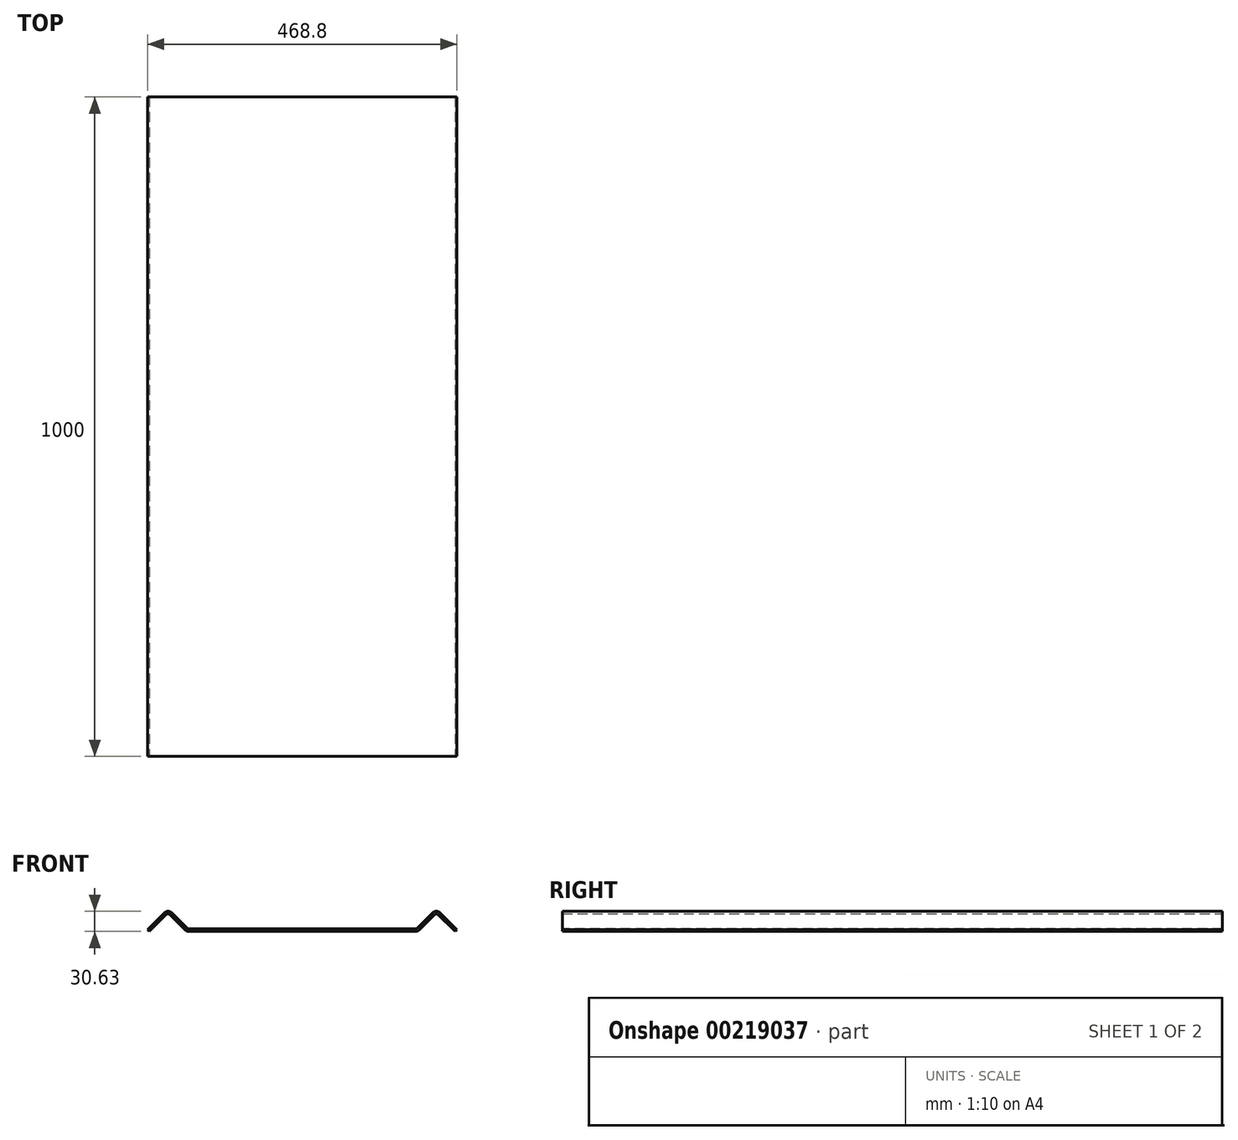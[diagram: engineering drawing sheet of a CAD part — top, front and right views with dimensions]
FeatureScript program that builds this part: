
annotation { "Feature Type Name" : "Feature", "Feature Type Description" : "" }
export const myFeature = defineFeature(function(context is Context, id is Id, definition is map)
    precondition{}
    {
        {
            var Q0;
            Q0=qCreatedBy(makeId("Front.planeOp"),FACE);
            var sketch = newSketch(context, id + "F0", { "sketchPlane" : qUnion([Q0])});
            skLineSegment(sketch, "E0", {"start": v(0, 0) * mm, "end": v(-175, 0) * mm});
            skLineSegment(sketch, "E1", {"start": v(-175, 0) * mm, "end": v(-203.28, 28.28) * mm});
            skLineSegment(sketch, "E2", {"start": v(-203.28, 28.28) * mm, "end": v(-231.57, 0) * mm});
            skLineSegment(sketch, "E3.0", {"start": v(-203.28, 33.94) * mm, "end": v(-234.4, 2.83) * mm});
            skLineSegment(sketch, "E3.1", {"start": v(-173.34, 4) * mm, "end": v(-203.28, 33.94) * mm});
            skLineSegment(sketch, "E3.2", {"start": v(0, 4) * mm, "end": v(-173.34, 4) * mm});
            skLineSegment(sketch, "E4", {"start": v(-231.57, 0) * mm, "end": v(-234.4, 2.83) * mm});
            skLineSegment(sketch, "E5", {"start": v(0, 0) * mm, "end": v(0, 19.74) * mm, "construction": true});
            skLineSegment(sketch, "E6.MirrorCS", {"start": v(231.57, 0) * mm, "end": v(234.4, 2.83) * mm});
            skLineSegment(sketch, "E7.MirrorCS", {"start": v(175, 0) * mm, "end": v(203.28, 28.28) * mm});
            skLineSegment(sketch, "E8.MirrorCS", {"start": v(203.28, 28.28) * mm, "end": v(231.57, 0) * mm});
            skLineSegment(sketch, "E9.MirrorCS", {"start": v(173.34, 4) * mm, "end": v(203.28, 33.94) * mm});
            skLineSegment(sketch, "E10.MirrorCS", {"start": v(0, 0) * mm, "end": v(175, 0) * mm});
            skLineSegment(sketch, "E11.MirrorCS", {"start": v(0, 4) * mm, "end": v(173.34, 4) * mm});
            skLineSegment(sketch, "E12.MirrorCS", {"start": v(203.28, 33.94) * mm, "end": v(234.4, 2.83) * mm});
            skSolve(sketch);
        }
        {
            var Q0;
            Q0 = qSketchRegion(id + "F0", true);
            extrude(context, id + "F1", {"entities" : qUnion([Q0]), "oppositeDirection" : true, "depth" : 1000 * mm});
        }
        {
            var Q0;
            Q0=makeQuery(id+"F1.opExtrude","SWEPT_EDGE",EDGE,{"disambiguationData":[OSD([sQuery(id+"F0.wireOp",EDGE,"E1"),sQuery(id+"F0.wireOp",EDGE,"E2")])]});
            var Q1;
            Q1=makeQuery(id+"F1.opExtrude","SWEPT_EDGE",EDGE,{"disambiguationData":[OSD([sQuery(id+"F0.wireOp",EDGE,"E7.MirrorCS"),sQuery(id+"F0.wireOp",EDGE,"E8.MirrorCS")])]});
            var Q2;
            Q2=makeQuery(id+"F1.opExtrude","SWEPT_EDGE",EDGE,{"disambiguationData":[OSD([sQuery(id+"F0.wireOp",EDGE,"E3.1"),sQuery(id+"F0.wireOp",EDGE,"E3.2")])]});
            var Q3;
            Q3=makeQuery(id+"F1.opExtrude","SWEPT_EDGE",EDGE,{"disambiguationData":[OSD([sQuery(id+"F0.wireOp",EDGE,"E9.MirrorCS"),sQuery(id+"F0.wireOp",EDGE,"E11.MirrorCS")])]});
            fillet(context, id + "F2", {"entities" : qUnion([Q0, Q1, Q2, Q3]), "radius" : 4 * mm, "tangentPropagation" : true, "allowEdgeOverflow" : false});
        }
        {
            var Q0;
            Q0=makeQuery(id+"F1.opExtrude","SWEPT_EDGE",EDGE,{"disambiguationData":[OSD([sQuery(id+"F0.wireOp",EDGE,"E3.0"),sQuery(id+"F0.wireOp",EDGE,"E3.1")])]});
            var Q1;
            Q1=makeQuery(id+"F1.opExtrude","SWEPT_EDGE",EDGE,{"disambiguationData":[OSD([sQuery(id+"F0.wireOp",EDGE,"E9.MirrorCS"),sQuery(id+"F0.wireOp",EDGE,"E12.MirrorCS")])]});
            var Q2;
            Q2=makeQuery(id+"F1.opExtrude","SWEPT_EDGE",EDGE,{"disambiguationData":[OSD([sQuery(id+"F0.wireOp",EDGE,"E0"),sQuery(id+"F0.wireOp",EDGE,"E1")])]});
            var Q3;
            Q3=makeQuery(id+"F1.opExtrude","SWEPT_EDGE",EDGE,{"disambiguationData":[OSD([sQuery(id+"F0.wireOp",EDGE,"E7.MirrorCS"),sQuery(id+"F0.wireOp",EDGE,"E10.MirrorCS")])]});
            fillet(context, id + "F3", {"entities" : qUnion([Q0, Q1, Q2, Q3]), "radius" : 8 * mm, "tangentPropagation" : true, "allowEdgeOverflow" : false});
        }
    });
